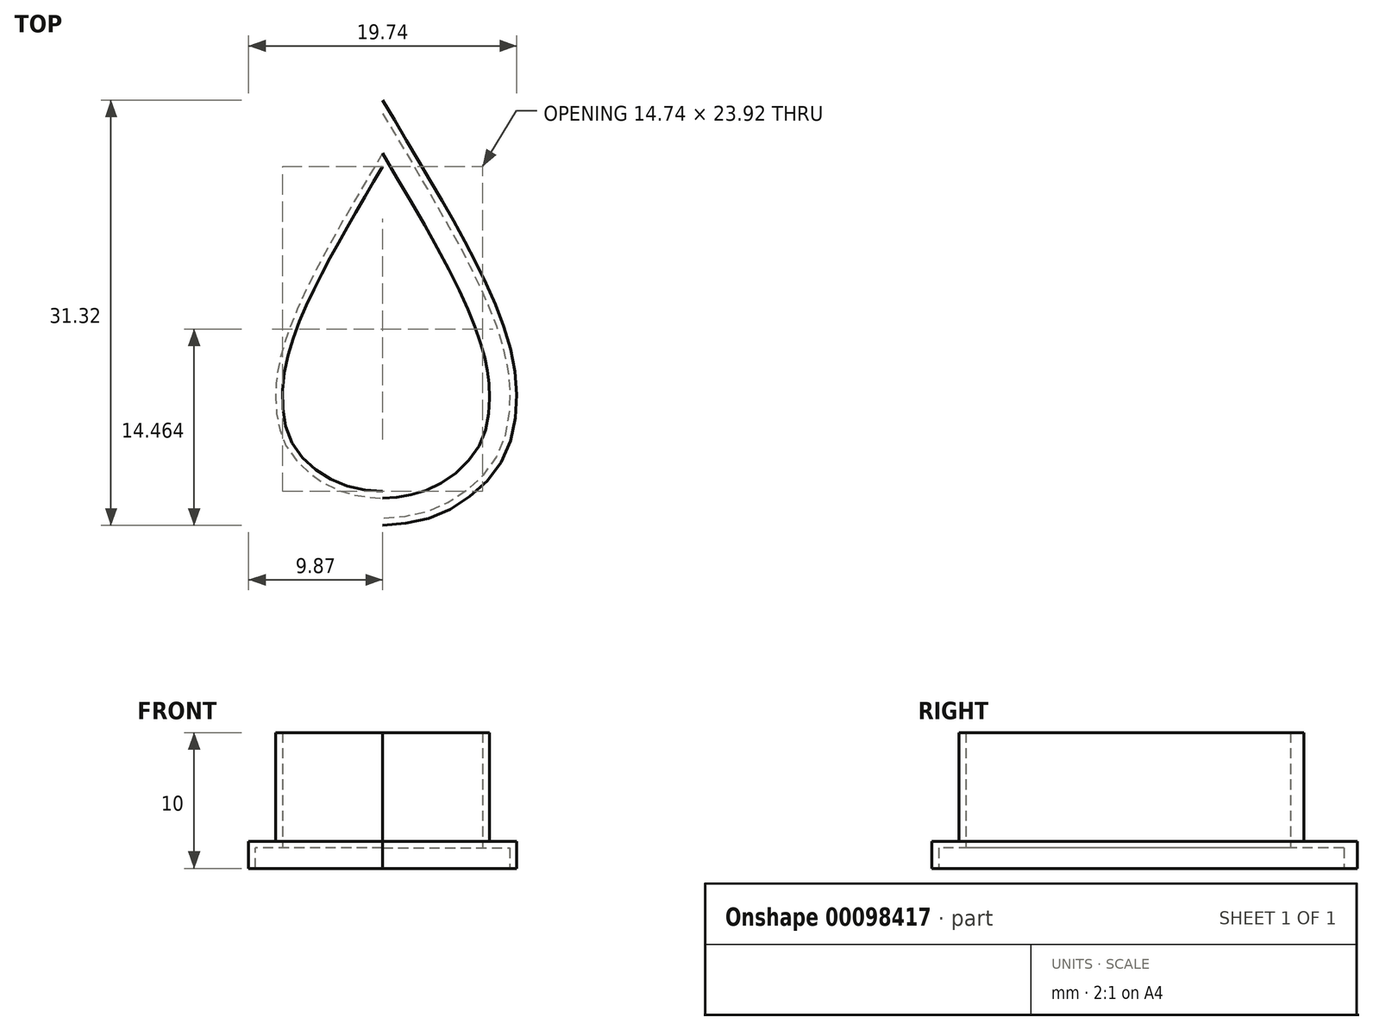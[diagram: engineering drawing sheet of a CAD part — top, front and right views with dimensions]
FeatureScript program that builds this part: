
annotation { "Feature Type Name" : "Feature", "Feature Type Description" : "" }
export const myFeature = defineFeature(function(context is Context, id is Id, definition is map)
    precondition{}
    {
        {
            var Q0;
            Q0=qCreatedBy(makeId("Top.planeOp"),FACE);
            var sketch = newSketch(context, id + "F0", { "sketchPlane" : qUnion([Q0])});
            skFitSpline(sketch, "E0", {"points": [v(0, 16.13) * mm, v(5.4, 6.54) * mm, v(7.43, 1.47) * mm, v(7.87, -1.45) * mm, v(7.07, -5.48) * mm, v(3.39, -8.62) * mm, v(0, -9.27) * mm], "startDerivative": vector(24.47, -41.24) * mm, "endDerivative": vector(-24.02, -1.68) * mm});
            skFitSpline(sketch, "E1.MirrorCS", {"points": [v(0, 16.13) * mm, v(-5.4, 6.54) * mm, v(-7.43, 1.47) * mm, v(-7.87, -1.45) * mm, v(-7.07, -5.48) * mm, v(-3.39, -8.62) * mm, v(0, -9.27) * mm], "startDerivative": vector(-24.47, -41.24) * mm, "endDerivative": vector(24.02, -1.68) * mm});
            skLineSegment(sketch, "E2", {"start": v(0, 16.13) * mm, "end": v(0, -9.27) * mm, "construction": true});
            skSolve(sketch);
        }
        {
            var Q0;
            Q0 = qSketchRegion(id + "F0", true);
            extrude(context, id + "F1", {"entities" : qUnion([Q0]), "depth" : 2 * mm});
        }
        {
            var Q0;
            Q0=makeQuery(id+"F1.opExtrude","SWEPT_BODY",BODY,{"disambiguationData":[OSD([sQuery(id+"F0.wireOp",EDGE,"E0"),sQuery(id+"F0.wireOp",EDGE,"E1.MirrorCS")])]});
            transform(context, id + "F2", {"entities" : qUnion([Q0]), "transformType" : TransformType.TRANSLATION_3D, "dx" : 0 * mm, "dy" : 0 * mm, "dz" : 0 * mm, "makeCopy" : true});
        }
        {
            var Q0;
            Q0=makeQuery(id+"F1.opExtrude","CAP_FACE",FACE,{"disambiguationData":[OSD([sQuery(id+"F0.wireOp",EDGE,"E0"),sQuery(id+"F0.wireOp",EDGE,"E1.MirrorCS")])],"isStart":true});
            var Q1;
            Q1=makeQuery(id+"F1.opExtrude","CAP_FACE",FACE,{"disambiguationData":[OSD([sQuery(id+"F0.wireOp",EDGE,"E0"),sQuery(id+"F0.wireOp",EDGE,"E1.MirrorCS")])],"isStart":false});
            shell(context, id + "F3", {"entities" : qUnion([Q0, Q1]), "thickness" : 2 * mm, "oppositeDirection" : true});
        }
        {
            var Q0;
            Q0=makeQuery(id+"F2.opPattern","COPY",FACE,{"derivedFrom":makeQuery(id+"F1.opExtrude","CAP_FACE",FACE,{"disambiguationData":[OSD([sQuery(id+"F0.wireOp",EDGE,"E0"),sQuery(id+"F0.wireOp",EDGE,"E1.MirrorCS")])],"isStart":false}),"instanceName":"1"});
            extrude(context, id + "F4", {"entities" : qUnion([Q0]), "operationType" : NewBodyOperationType.ADD, "depth" : 8 * mm});
        }
        {
            var Q0;
            Q0=makeQuery(id+"F4.opExtrude","CAP_FACE",FACE,{"disambiguationData":[OSD([sQuery(id+"F0.wireOp",EDGE,"E0"),sQuery(id+"F0.wireOp",EDGE,"E1.MirrorCS")])],"isStart":false});
            var Q1;
            Q1=makeQuery(id+"F2.opPattern","COPY",FACE,{"derivedFrom":makeQuery(id+"F1.opExtrude","CAP_FACE",FACE,{"disambiguationData":[OSD([sQuery(id+"F0.wireOp",EDGE,"E0"),sQuery(id+"F0.wireOp",EDGE,"E1.MirrorCS")])],"isStart":true}),"instanceName":"1"});
            shell(context, id + "F5", {"entities" : qUnion([Q0, Q1]), "thickness" : .5 * mm});
        }
    });
